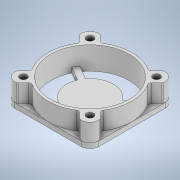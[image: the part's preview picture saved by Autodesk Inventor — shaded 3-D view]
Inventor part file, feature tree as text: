
AUTODESK INVENTOR PART (.ipt)
format: ipt  version: 2022 (Build 260153000, 153)  size: 268,288 bytes
history: native  units: in
note: dims shown in document units (in); Inventor stores cm internally (conversion verified against a paired STEP export)
features: extrude x2, sketch x2, fillet x1
ambient origin geometry x8: Origin, YZ Plane, XZ Plane, XY Plane, X Axis, Y Axis, Z Axis, Center Point
bodies: Solid1 (feature_tree)
feature tree (5):
  extrude  "Extrusion1"  Depth=1.595in
  extrude  "Extrusion2"  Depth=0.17in
  fillet  "Fillet2"  Radius=0.88in
  sketch  "Sketch1"  dims[d0=1.595in d1=1.595in]
  sketch  "Sketch2"  dims[d2=1.49in d3=0.17in d4=0.88in d5=0.055in d6=0.055in d7=1.1811in d9=360.0deg d11=0.095in d12=0.0in d16=0.34in d17=0.0in d25=0.565in d26=0.565in d27=0.135in d28=0.135in d29=135.0deg d30=1.5748in d32=360.0deg d34=0.05in]
